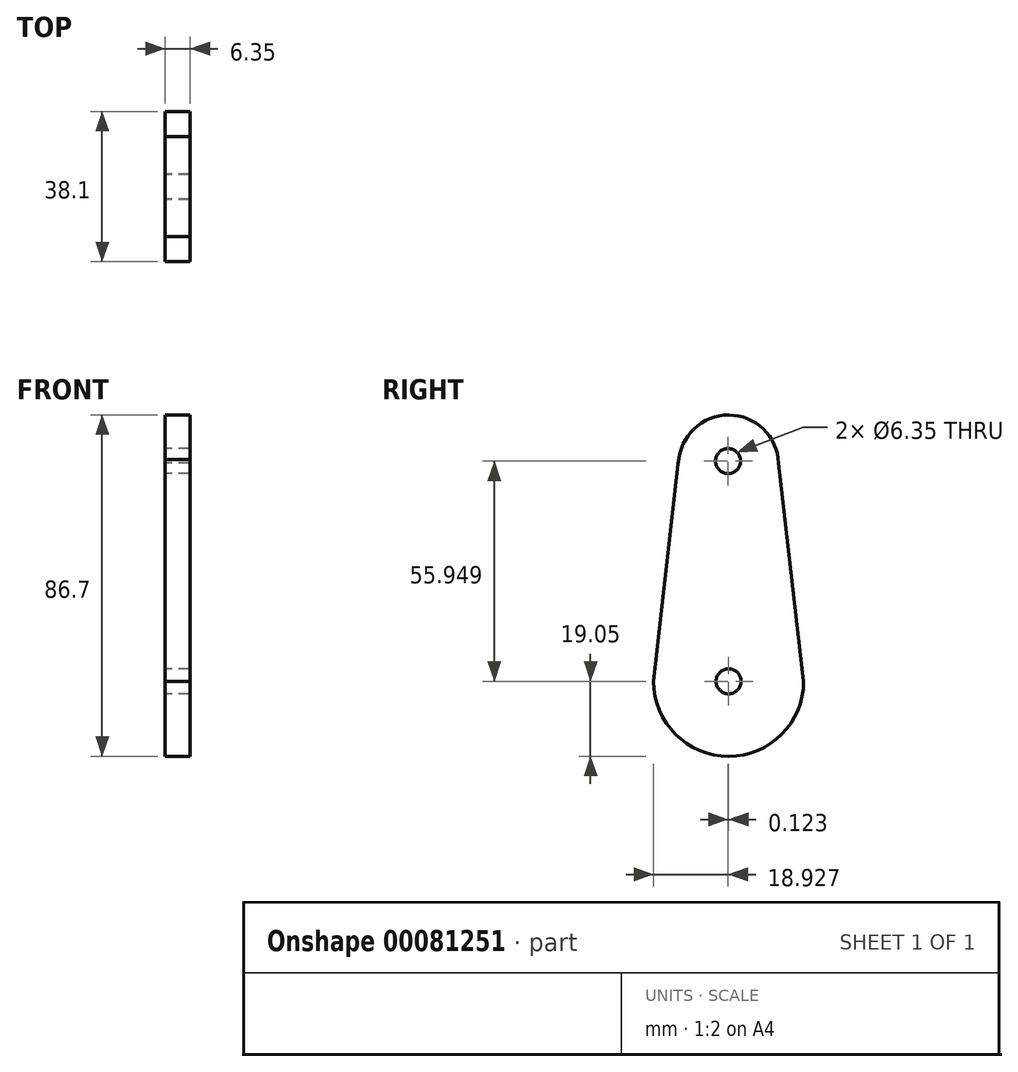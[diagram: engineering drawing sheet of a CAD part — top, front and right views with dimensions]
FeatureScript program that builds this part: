
annotation { "Feature Type Name" : "Feature", "Feature Type Description" : "" }
export const myFeature = defineFeature(function(context is Context, id is Id, definition is map)
    precondition{}
    {
        {
            var Q0;
            Q0=qCreatedBy(makeId("Right.planeOp"),FACE);
            var sketch = newSketch(context, id + "F0", { "sketchPlane" : qUnion([Q0])});
            skArc(sketch, "E0", {"start": v(-19.05, 0) * mm, "mid": v(0, -19.05) * mm, "end": v(19.05, 0) * mm});
            skLineSegment(sketch, "E1", {"start": v(-12.7, 58.77) * mm, "end": v(-12.7, 22.15) * mm, "construction": true});
            skLineSegment(sketch, "E2", {"start": v(12.7, 69.84) * mm, "end": v(12.7, 46.56) * mm, "construction": true});
            skArc(sketch, "E3", {"start": v(-12.7, 56.4) * mm, "mid": v(-12.7, 55.95) * mm, "end": v(-12.7, 55.5) * mm});
            skLineSegment(sketch, "E4", {"start": v(-12.7, 56.4) * mm, "end": v(-19.05, 0) * mm});
            skLineSegment(sketch, "E5", {"start": v(12.7, 55.42) * mm, "end": v(19.05, 0) * mm});
            skPoint(sketch, "E6.orphan", {"position": v(0, 68.53) * mm});
            skArc(sketch, "E7", {"start": v(12.7, 55.42) * mm, "mid": v(0.04, 67.65) * mm, "end": v(-12.7, 55.5) * mm});
            skCircle(sketch, "E8", {"center": v(-0.12, 55.95) * mm, "radius": 3.18 * mm});
            skCircle(sketch, "E9", {"center": v(0, 0) * mm, "radius": 3.18 * mm});
            skSolve(sketch);
        }
        {
            var Q0;
            Q0 = qSketchRegion(id + "F0", true);
            extrude(context, id + "F1", {"entities" : qUnion([Q0]), "depth" : 6.35 * mm});
        }
    });
